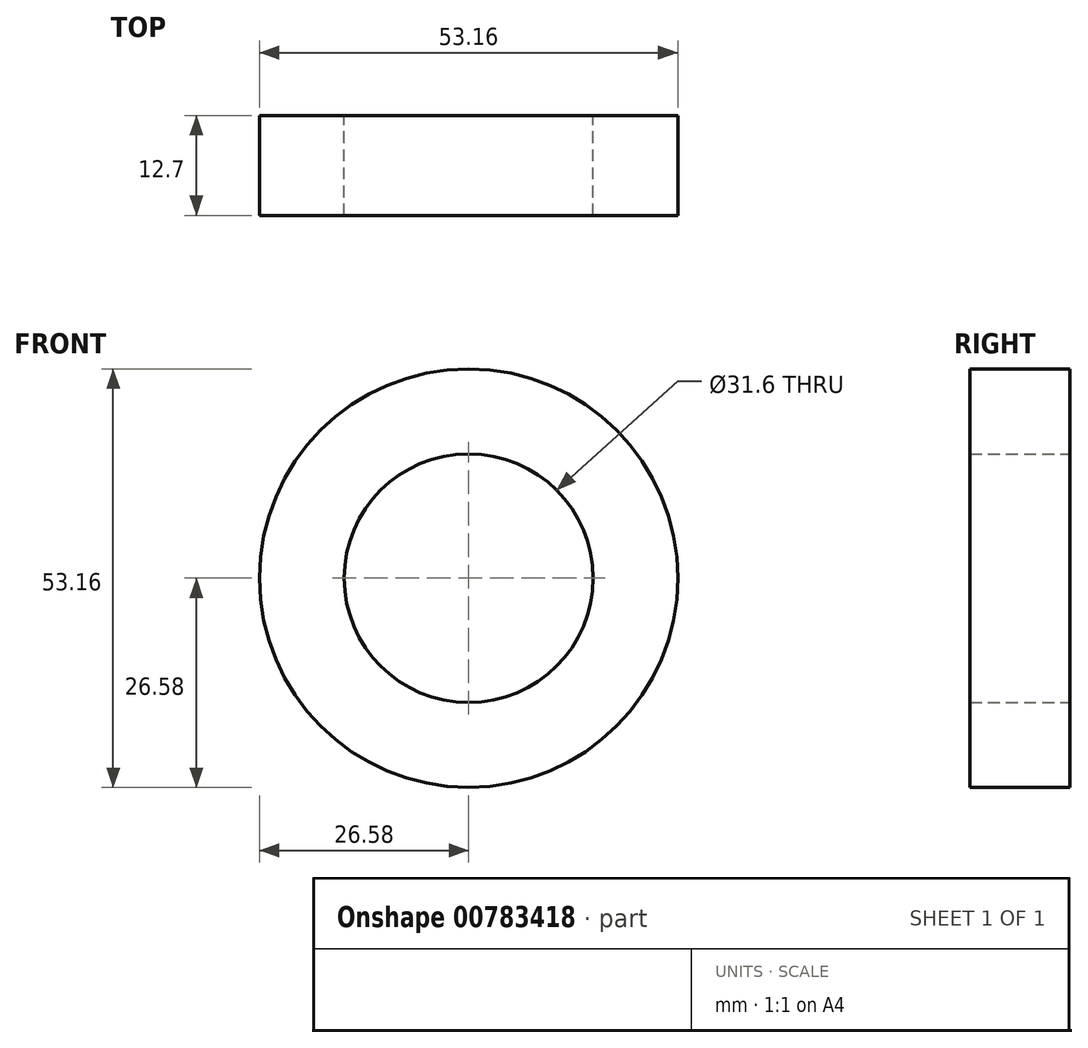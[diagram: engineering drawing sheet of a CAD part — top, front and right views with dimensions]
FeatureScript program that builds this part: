
annotation { "Feature Type Name" : "Feature", "Feature Type Description" : "" }
export const myFeature = defineFeature(function(context is Context, id is Id, definition is map)
    precondition{}
    {
        {
            var Q0;
            Q0=qCreatedBy(makeId("Front.planeOp"),FACE);
            var sketch = newSketch(context, id + "F0", { "sketchPlane" : qUnion([Q0])});
            skCircle(sketch, "E0", {"center": v(0, 0) * mm, "radius": 26.58 * mm});
            skSolve(sketch);
        }
        {
            var Q0;
            Q0=makeQuery(id+"F0.imprint","IMPRINT",FACE,{"disambiguationData":[TD([[makeQuery(id+"F0.imprint","IMPRINT",EDGE,{"derivedFrom":sQuery(id+"F0.wireOp",EDGE,"E0")}),1.0]])]});
            extrude(context, id + "F1", {"entities" : qUnion([Q0]), "endBound" : BoundingType.SYMMETRIC, "depth" : 12.7 * mm, "offsetDistance" : 25.4 * mm});
        }
        {
            var Q0;
            Q0=qCreatedBy(makeId("Top.planeOp"),FACE);
            var sketch = newSketch(context, id + "F2", { "sketchPlane" : qUnion([Q0])});
            skCircle(sketch, "E1", {"center": v(0, 0) * mm, "radius": 8.33 * mm});
            skSolve(sketch);
        }
        {
            var Q0;
            Q0=sQuery(id+"F2.wireOp",EDGE,"E1");
            extrude(context, id + "F3", {"bodyType" : ToolBodyType.SURFACE, "surfaceEntities" : qUnion([Q0]), "depth" : 101.6 * mm, "offsetDistance" : 25.4 * mm, "hasSecondDirection" : true, "secondDirectionOppositeDirection" : false, "secondDirectionDepth" : 25.4 * mm});
        }
        {
            var Q0;
            Q0=qCreatedBy(makeId("Front.planeOp"),FACE);
            var sketch = newSketch(context, id + "F4", { "sketchPlane" : qUnion([Q0])});
            skCircle(sketch, "E2", {"center": v(0, 0) * mm, "radius": 15.8 * mm});
            skSolve(sketch);
        }
        {
            var Q0;
            Q0 = qSketchRegion(id + "F4", true);
            extrude(context, id + "F5", {"entities" : qUnion([Q0]), "operationType" : NewBodyOperationType.REMOVE, "endBound" : BoundingType.SYMMETRIC, "depth" : 76.2 * mm, "offsetDistance" : 25.4 * mm});
        }
    });
